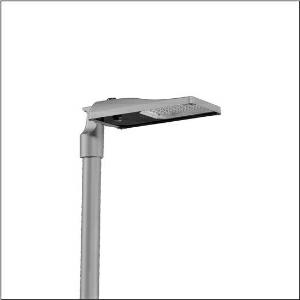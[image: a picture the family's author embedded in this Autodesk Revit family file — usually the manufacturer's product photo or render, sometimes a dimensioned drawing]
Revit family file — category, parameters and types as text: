
# Revit family: streetlight_sl_31_mini___st1_0a_5xh6d3at08ja_2b3a
name_source: partatom
category: Lighting Fixtures
units: mm (PartAtom-declared; Revit-internal decimal feet)

## family parameters
Cut with Voids When Loaded = No
Host = Face
Light Source = No
Part Type = Normal
Room Calculation Point = No
Round Connector Dimension = Use Diameter
Shared = No

## types (1)
- --- (1 x LED, 12270 lm, 82.5 W, 3000K)
    Apparent Load = 83 VA
    CIE Flux Codes = 40 73 97 100 100
    Color Rendering = 70
    Color Temperature = 3000K
    Default Elevation = 1800 mm
    Description = Streetlight SL 31 mini D4i mast luminaire for post-top, side-entry; light control with lens of PMMA; light distribution: ST1.0a, direct asymmetric distribution, for standard-compliant lighting for roads and squares; LED: luminous flux: 12.270lm, light colour: 730, colour temperature: 3000K; luminous efficacy: 148,7lm/W; control: pre-setting: logarithmic dimming characteristic, flexible luminous flux parameterisation, time-dependent luminous flux control, constant luminous flux control, power reduction, intelligent temperature release in ECG and LED module, overheat protection; luminaire housing, of diecast aluminium, Siteco® metallic grey (DB 702S), corrosivity category C5 high according to DIN EN ISO 12944; cover of toughened safety glass, transparent, opened without tools; mast flange of diecast aluminium, Siteco® metallic grey (DB 702S), spigot size: 76/60mm, mast flange included unmounted; with cable H07RN-F 2x 1.5mm², cable length: 10,5m, connection cable pre-assembled; mains connection: 220..240V, AC, 50/60Hz; power consumption (at start of service life): 82,5W / (at end of service life): 90,1W / (with reduced operation 50%): 36,8W; protection rating (complete): IP66; insulation class (complete): insulation class II (safety insulation); impact resistance: IK09; certification: CE, ENEC, ENEC+, VDE, UKCA, ZD4i; permissible operating ambient temperature for outdoor applications: -40..+50°C; packaging unit: 1 piece

Light Distribution: ST1.0a
    Height = 76 mm
    Lamp = 1 x LED
    Lamp Light Flux = 12270 lm
    Lamp Power = 82.5 W
    Lamp count = 1
    Length = 547 mm
    Luminous efficacy = 149 lm/W
    Manufacturer = Siteco
    ModVariant = No
    Model = 5XH6D3AT08JA
    Number of Poles = 1
    OnlyDefault = Yes
    Power Factor = 1
    Product Name = Streetlight SL 31 mini | ST1.0a
    Product group = mast luminaire | pylon top
    ProductGroupID = 6100
    Protection Class = Protection class II
    Protection Degree = IP 66
    RLX_Detail_Level = 1
    RLX_Emergency_Light_Flux = 0 lm
    RLX_Emergency_Type = 0
    RLX_Emergency_Type_DB = No
    RlxData = <blob elided: 39833 chars, md5=1182553c>
    Socket = socket
    Standby Power = 0 W
    System Light Flux = 12270 lm
    System Power = 83 W
    Type Comments = factory setting: luminous flux: 100 % | dim-lin: 254 | 870 mA
    Type Image = l_1300332.jpg
    URL = http://relux.com
    VarID = @adj_050166
    Voltage = 0 V
    Weight = 0.00 kg
    Width = 265 mm

## geometry (parser evidence)
native form markers: Blend x4, Sweep x11
no freeform markers — native parametric forms only
